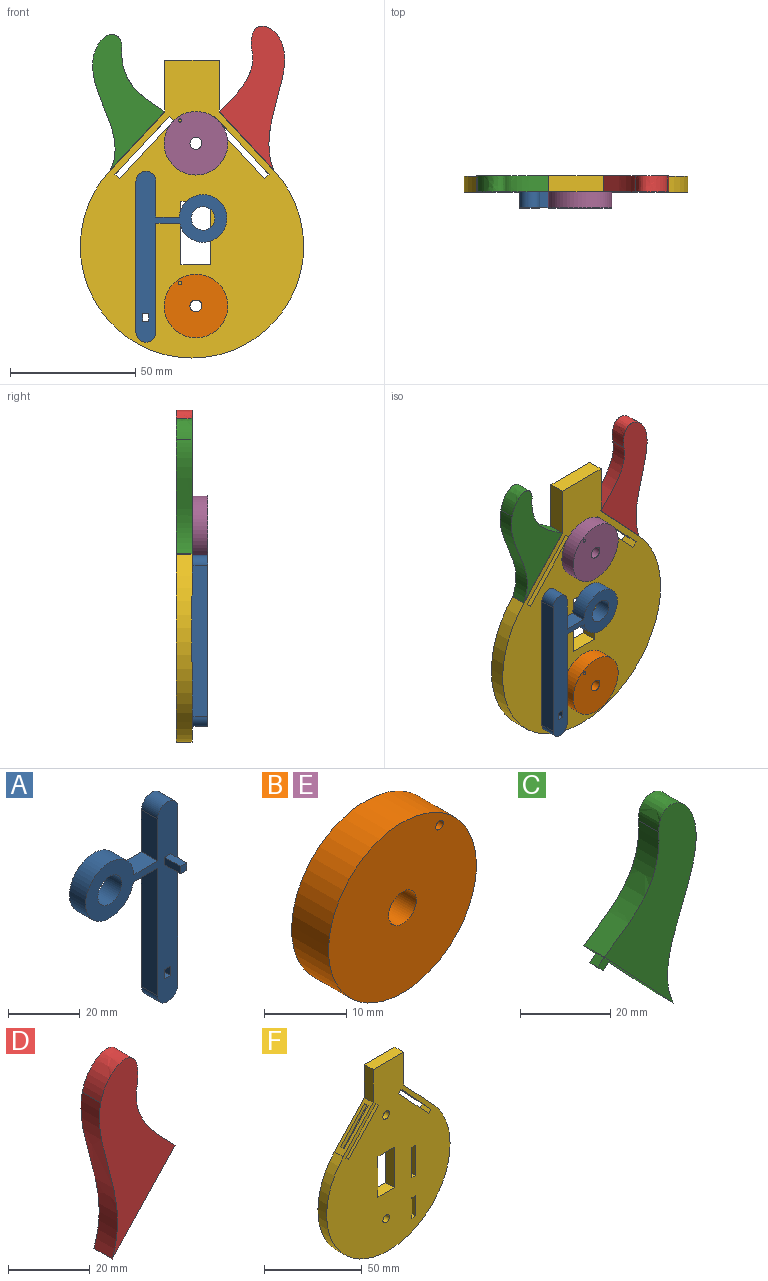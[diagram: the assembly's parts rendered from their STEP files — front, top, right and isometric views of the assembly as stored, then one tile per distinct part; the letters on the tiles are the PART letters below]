
ASSEMBLY  parts=6 mates=5
PART A: 20 faces, bbox 36.3x12.6x68.3 mm
  f0: plane 6.35x3.18mm, normal (-1,0,0), area 20.2mm2, adj f1,f12,f13,f14
  f1: plane 6.35x2.41mm, normal (0,0,1), area 15.3mm2, adj f0,f2,f13,f14
  f2: plane 6.35x3.18mm, normal (1,0,0), area 20.2mm2, adj f1,f12,f13,f14
  f3: cylinder r=9.53mm len=19.05mm, axis (0,1,0), area 364.3mm2, adj f4,f10,f13,f14
  f4: plane 9.53x6.35mm, normal (0,0,-1), area 60.5mm2, adj f3,f5,f13,f14
  f5: plane 43.57x6.35mm, normal (-1,0,0), area 276.7mm2, adj f4,f6,f13,f14
  f6: cylinder r=3.97mm len=7.94mm, axis (0,1,0), area 79.2mm2, adj f5,f7,f13,f14
  f7: plane 60.33x6.35mm, normal (1,0,0), area 383.1mm2, adj f6,f8,f13,f14
  f8: cylinder r=3.97mm len=7.94mm, axis (0,1,0), area 79.2mm2, adj f7,f9,f13,f14
  f9: plane 14.29x6.35mm, normal (-1,0,0), area 90.7mm2, adj f8,f10,f13,f14
  f10: plane 9.35x6.35mm, normal (0,0,1), area 59.4mm2, adj f3,f9,f13,f14
  f11: cylinder r=4.7mm len=9.4mm, axis (0,1,0), area 187.6mm2, adj f13,f14
  f12: plane 6.35x2.41mm, normal (0,0,-1), area 15.3mm2, adj f0,f2,f13,f14
  f13: plane 68.26x36.32mm, normal (0,-1,0), area 753.2mm2, adj f0,f1,f2,f3,f4,f5,f6,f7
  f14: plane 68.26x36.32mm, normal (0,1,0), area 759.3mm2, adj f0,f1,f2,f3,f4,f5,f6,f7
  f15: plane 6.22x2.41mm, normal (0,0,-1), area 15mm2, adj f13,f16,f18,f19
  f16: plane 6.22x2.54mm, normal (-1,0,0), area 15.8mm2, adj f13,f15,f17,f19
  f17: plane 6.22x2.41mm, normal (0,0,1), area 15mm2, adj f13,f16,f18,f19
  f18: plane 6.22x2.54mm, normal (1,0,0), area 15.8mm2, adj f13,f15,f17,f19
  f19: plane 2.54x2.41mm, normal (0,-1,0), area 6.1mm2, adj f15,f16,f17,f18
PART B: 5 faces, bbox 25.4x6.4x25.4 mm
  f0: cylinder r=2.39mm len=6.35mm, axis (0,1,0), area 95.3mm2, adj f3,f4
  f1: cylinder r=0.65mm len=6.35mm, axis (0,1,0), area 25.9mm2, adj f3,f4
  f2: cylinder r=12.7mm len=25.4mm, axis (0,1,0), area 506.7mm2, adj f3,f4
  f3: plane 25.4x25.4mm, normal (0,-1,0), area 487.5mm2, adj f0,f1,f2
  f4: plane 25.4x25.4mm, normal (0,1,0), area 487.5mm2, adj f0,f1,f2
PART C: 11 faces, bbox 30.7x6.4x55.6 mm
  f0: plane 23.22x21.65mm, normal (-0.73,0,-0.68), area 195.3mm2, adj f1,f3,f4,f5,f6,f7,f8,f9
  f1: extruded ~45.61x8.95mm, area 300.4mm2, adj f0,f2,f4,f5
  f2: extruded ~11.29x8.5mm, area 124.8mm2, adj f1,f3,f4,f5
  f3: extruded ~25.38x17.18mm, area 207mm2, adj f0,f2,f4,f5
  f4: plane 55.56x30.64mm, normal (0,-1,0), area 653.1mm2, adj f0,f1,f2,f3
  f5: plane 55.56x30.64mm, normal (0,1,0), area 653.1mm2, adj f0,f1,f2,f3
  f6: plane 3.59x3.59mm, normal (0,-1,0), area 6.5mm2, adj f0,f7,f9,f10
  f7: plane 2.49x1.86mm, normal (-0.68,0,0.73), area 6.3mm2, adj f0,f6,f8,f10
  f8: plane 3.59x3.59mm, normal (0,1,0), area 6.5mm2, adj f0,f7,f9,f10
  f9: plane 2.49x1.86mm, normal (0.68,0,-0.73), area 6.3mm2, adj f0,f6,f8,f10
  f10: plane 2.49x1.86mm, normal (-0.73,0,-0.68), area 6.3mm2, adj f6,f7,f8,f9
PART D: 11 faces, bbox 27.7x6.4x59.9 mm
  f0: extruded ~48.63x6.35mm, area 314.7mm2, adj f1,f3,f4,f5
  f1: plane 23.22x21.65mm, normal (0.73,0,-0.68), area 195.2mm2, adj f0,f2,f4,f5,f6,f7,f8,f9
  f2: extruded ~24.49x13.39mm, area 184.4mm2, adj f1,f3,f4,f5
  f3: extruded ~12.86x9.78mm, area 159.7mm2, adj f0,f2,f4,f5
  f4: plane 59.88x27.67mm, normal (0,-1,0), area 699.5mm2, adj f0,f1,f2,f3
  f5: plane 59.88x27.67mm, normal (0,1,0), area 699.5mm2, adj f0,f1,f2,f3
  f6: plane 3.59x3.59mm, normal (0,1,0), area 6.5mm2, adj f1,f7,f9,f10
  f7: plane 2.51x1.86mm, normal (0.68,0,0.73), area 6.4mm2, adj f1,f6,f8,f10
  f8: plane 3.59x3.59mm, normal (0,-1,0), area 6.5mm2, adj f1,f7,f9,f10
  f9: plane 2.51x1.86mm, normal (-0.68,0,-0.73), area 6.4mm2, adj f1,f6,f8,f10
  f10: plane 2.51x1.86mm, normal (0.73,0,-0.68), area 6.4mm2, adj f6,f7,f8,f9
PART E: same geometry as B
PART F: 38 faces, bbox 89.2x6.4x118.9 mm
  f0: plane 23.22x21.65mm, normal (0.73,0,0.68), area 137.1mm2, adj f4,f5,f28,f29,f34,f35,f36,f37
  f1: plane 23.22x21.65mm, normal (-0.73,0,-0.68), area 137.1mm2, adj f12,f13,f28,f29,f34,f35,f36,f37
  f2: plane 23.22x21.65mm, normal (-0.73,0,0.68), area 137.1mm2, adj f4,f27,f28,f29,f30,f31,f32,f33
  f3: plane 23.22x21.65mm, normal (0.73,0,-0.68), area 137.1mm2, adj f10,f21,f28,f29,f30,f31,f32,f33
  f4: cylinder r=44.61mm len=89.22mm, axis (0,1,0), area 1315mm2, adj f0,f2,f28,f29
  f5: plane 20.64x6.35mm, normal (1,0,0), area 131mm2, adj f0,f6,f28,f29
  f6: plane 21.95x6.35mm, normal (0,0,1), area 139.4mm2, adj f5,f27,f28,f29
  f7: plane 18.9x6.35mm, normal (1,0,0), area 120mm2, adj f8,f20,f28,f29
  f8: plane 6.35x2.79mm, normal (0,0,-1), area 17.7mm2, adj f7,f9,f28,f29
  f9: plane 18.9x6.35mm, normal (-1,0,0), area 120mm2, adj f8,f20,f28,f29
  f10: plane 6.35x1.86mm, normal (-0.68,0,-0.73), area 16.1mm2, adj f3,f11,f28,f29
  f11: plane 23.22x21.65mm, normal (-0.73,0,0.68), area 201.6mm2, adj f10,f21,f28,f29
  f12: plane 6.35x1.86mm, normal (0.68,0,-0.73), area 16.1mm2, adj f1,f22,f28,f29
  f13: plane 6.35x1.86mm, normal (-0.68,0,0.73), area 16.1mm2, adj f1,f22,f28,f29
  f14: plane 6.35x2.79mm, normal (0,0,-1), area 17.7mm2, adj f15,f25,f28,f29
  f15: plane 12.7x6.35mm, normal (-1,0,0), area 80.6mm2, adj f14,f16,f28,f29
  f16: plane 6.35x2.79mm, normal (0,0,1), area 17.7mm2, adj f15,f25,f28,f29
  f17: plane 11.96x6.35mm, normal (0,0,-1), area 76mm2, adj f18,f26,f28,f29
  f18: plane 25.4x6.35mm, normal (-1,0,0), area 161.3mm2, adj f17,f19,f28,f29
  f19: plane 11.96x6.35mm, normal (0,0,1), area 76mm2, adj f18,f26,f28,f29
  f20: plane 6.35x2.79mm, normal (0,0,1), area 17.7mm2, adj f7,f9,f28,f29
  f21: plane 6.35x1.86mm, normal (0.68,0,0.73), area 16.1mm2, adj f3,f11,f28,f29
  f22: plane 23.22x21.65mm, normal (0.73,0,0.68), area 201.6mm2, adj f12,f13,f28,f29
  f23: cylinder r=2.39mm len=6.35mm, axis (0,1,0), area 95.3mm2, adj f28,f29
  f24: cylinder r=2.39mm len=6.35mm, axis (0,1,0), area 95.3mm2, adj f28,f29
  f25: plane 12.7x6.35mm, normal (1,0,0), area 80.6mm2, adj f14,f16,f28,f29
  f26: plane 25.4x6.35mm, normal (1,0,0), area 161.3mm2, adj f17,f19,f28,f29
  f27: plane 20.64x6.35mm, normal (-1,0,0), area 131mm2, adj f2,f6,f28,f29
  f28: plane 118.89x89.22mm, normal (0,-1,0), area 6487.9mm2, adj f0,f1,f2,f3,f4,f5,f6,f7
  f29: plane 118.89x89.22mm, normal (0,1,0), area 6487.9mm2, adj f0,f1,f2,f3,f4,f5,f6,f7
  f30: plane 2.54x1.86mm, normal (-0.68,0,-0.73), area 6.5mm2, adj f2,f3,f31,f33
  f31: plane 20.31x19.18mm, normal (0,-1,0), area 64.5mm2, adj f2,f3,f30,f32
  f32: plane 2.54x1.86mm, normal (0.68,0,0.73), area 6.5mm2, adj f2,f3,f31,f33
  f33: plane 20.31x19.18mm, normal (0,1,0), area 64.5mm2, adj f2,f3,f30,f32
  f34: plane 2.54x1.86mm, normal (0.68,0,-0.73), area 6.5mm2, adj f0,f1,f35,f37
  f35: plane 20.31x19.18mm, normal (0,1,0), area 64.5mm2, adj f0,f1,f34,f36
  f36: plane 2.54x1.86mm, normal (-0.68,0,0.73), area 6.5mm2, adj f0,f1,f35,f37
  f37: plane 20.31x19.18mm, normal (0,-1,0), area 64.5mm2, adj f0,f1,f34,f36
PLACE A rot(axis=(0,0,1),180deg) t=(-38.76,-25.2,-28.15)mm
PLACE B rot(axis=(0,0,-1),180deg) t=(-18.79,-25.27,-47.81)mm
PLACE C rot(axis=(0,0,1),180deg) t=(-18.71,-18.92,6.53)mm
PLACE D rot(axis=(0,0,1),180deg) t=(-18.87,-18.92,6.53)mm
PLACE E rot(axis=(0,0,1),180deg) t=(-18.79,-25.27,17.18)mm
PLACE F rot(axis=(0,0,1),180deg) t=(-18.79,-18.92,6.44)mm fixed
MATE revolute B.f0 <-> F.f24  axis (0,1,0) through (-18.79,-22.09,-47.81)mm
MATE pin_slot F.f2 <-> D.f1  axis (0.73,0,0.68) through (1.62,-18.92,17.85)mm
MATE revolute F.f23 <-> E.f2  axis (0,-1,0) through (-18.79,-22.09,17.18)mm
MATE pin_slot F.f0 <-> C.f0  axis (-0.73,0,0.68) through (-42.35,-18.92,17.85)mm
MATE slider F.f8 <-> A.f17  axis (0,0,-1) through (-38.76,-18.92,-12.4)mm
